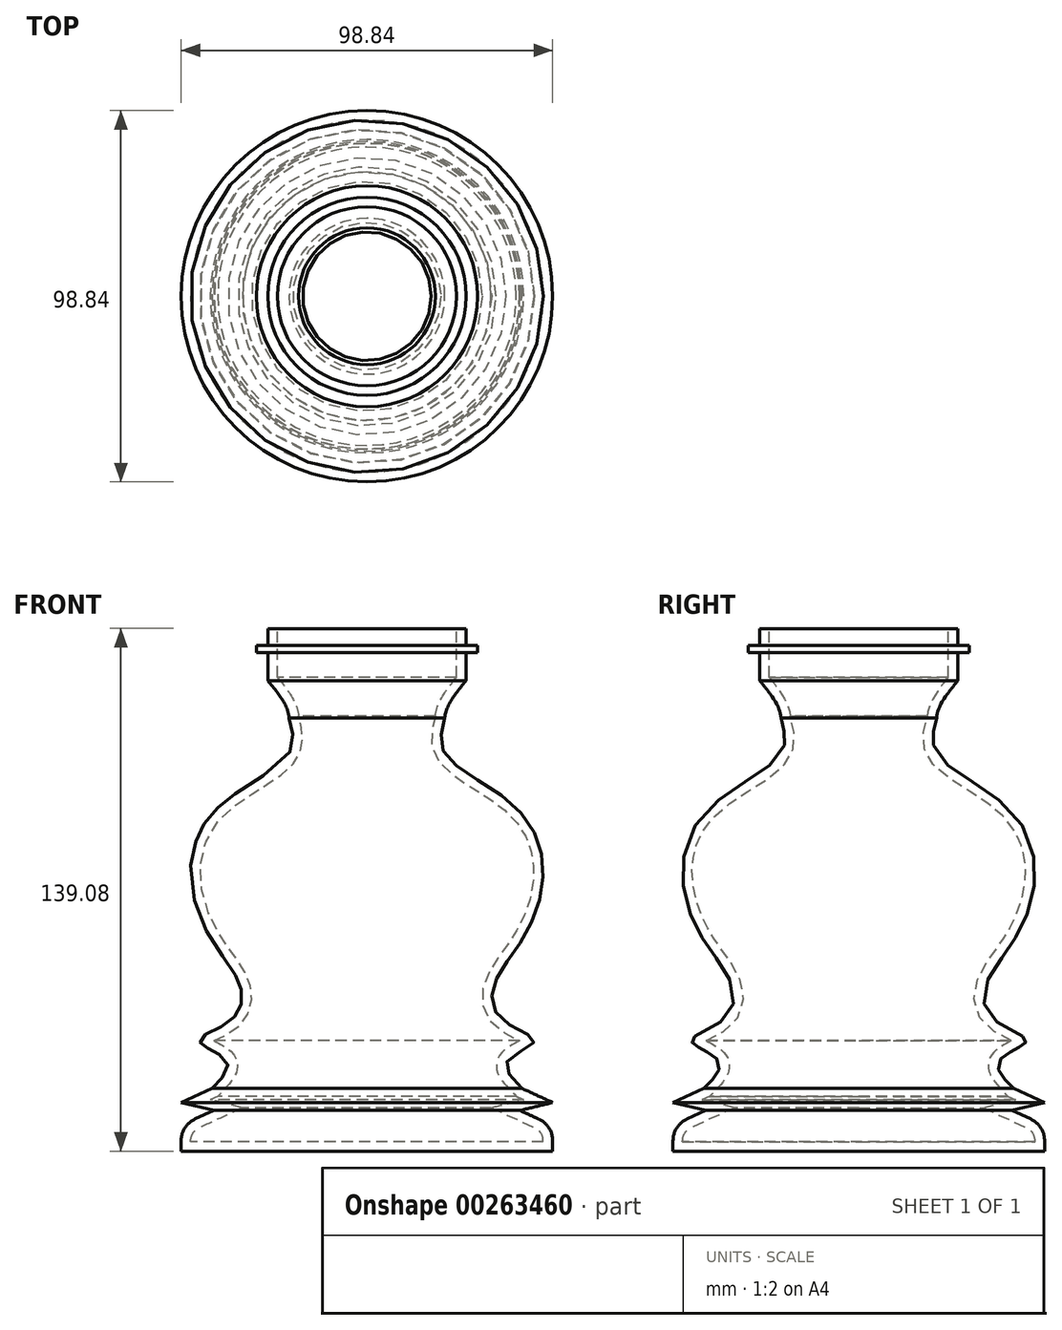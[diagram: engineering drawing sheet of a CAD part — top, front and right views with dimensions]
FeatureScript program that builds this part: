
annotation { "Feature Type Name" : "Feature", "Feature Type Description" : "" }
export const myFeature = defineFeature(function(context is Context, id is Id, definition is map)
    precondition{}
    {
        {
            var Q0;
            Q0=qCreatedBy(makeId("Front.planeOp"),FACE);
            var sketch = newSketch(context, id + "F0", { "sketchPlane" : qUnion([Q0])});
            skLineSegment(sketch, "E0", {"start": v(0, -75.54) * mm, "end": v(-49.42, -75.54) * mm});
            skLineSegment(sketch, "E1", {"start": v(-49.42, -75.54) * mm, "end": v(-49.42, -72.79) * mm});
            skLineSegment(sketch, "E2", {"start": v(-45.72, -67.01) * mm, "end": v(-40.71, -64.71) * mm});
            skLineSegment(sketch, "E3", {"start": v(-40.71, -64.71) * mm, "end": v(-49.42, -62.6) * mm});
            skLineSegment(sketch, "E4", {"start": v(-49.42, -62.6) * mm, "end": v(-41.18, -58.83) * mm});
            skFitSpline(sketch, "E5", {"points": [v(-49.42, -45.42) * mm, v(-39.06, -34.6) * mm, v(-49.42, -13.18) * mm, v(-42.36, 18.6) * mm, v(-25.65, 31.77) * mm, v(-20.7, 39.77) * mm, v(-26.36, 49.65) * mm], "startDerivative": vector(101.2, 64.64) * mm, "endDerivative": vector(-62.4, 76.27) * mm});
            skLineSegment(sketch, "E6", {"start": v(-26.36, 49.65) * mm, "end": v(-26.36, 57.18) * mm});
            skLineSegment(sketch, "E7", {"start": v(-26.36, 57.18) * mm, "end": v(-29.42, 57.18) * mm});
            skLineSegment(sketch, "E8", {"start": v(-29.42, 57.18) * mm, "end": v(-29.42, 59.07) * mm});
            skLineSegment(sketch, "E9", {"start": v(-29.42, 59.07) * mm, "end": v(-26.36, 59.07) * mm});
            skLineSegment(sketch, "E10", {"start": v(-26.36, 59.07) * mm, "end": v(-26.36, 63.54) * mm});
            skLineSegment(sketch, "E11", {"start": v(-26.36, 63.54) * mm, "end": v(0, 63.54) * mm});
            skLineSegment(sketch, "E12", {"start": v(0, 63.54) * mm, "end": v(0, -75.54) * mm});
            skPoint(sketch, "E13.visualSharp", {"position": v(-49.42, -56.24) * mm});
            skPoint(sketch, "E14.visualSharp", {"position": v(-49.42, -68.71) * mm});
            skArc(sketch, "E14.filletArc", {"start": v(-45.72, -67.01) * mm, "mid": v(-48.41, -69.36) * mm, "end": v(-49.42, -72.79) * mm});
            skFitSpline(sketch, "E15", {"points": [v(-20.7, 39.77) * mm, v(-20.7, 30.3) * mm, v(-38.75, 16.74) * mm, v(-46.88, 0) * mm, v(-41.88, -18.4) * mm, v(-33.61, -31.79) * mm, v(-36.23, -40.76) * mm, v(-44.53, -46.27) * mm, v(-37.32, -51.58) * mm, v(-41.18, -58.83) * mm], "startDerivative": vector(28.95, -103.5) * mm, "endDerivative": vector(-87.82, -88) * mm});
            skPoint(sketch, "E13.filletArc.center.orphan", {"position": v(-43.07, -51.58) * mm});
            skSolve(sketch);
        }
        {
            var Q0;
            Q0=makeQuery(id+"F0.imprint","IMPRINT",FACE,{"disambiguationData":[TD([[makeQuery(id+"F0.imprint","IMPRINT",EDGE,{"derivedFrom":sQuery(id+"F0.wireOp",EDGE,"E0")}),-1.0]])]});
            var Q1;
            Q1=sQuery(id+"F0.wireOp",EDGE,"E12");
            revolve(context, id + "F1", {"entities" : qUnion([Q0]), "axis" : qUnion([Q1]), "revolveType" : RevolveType.FULL});
        }
        {
            var Q0;
            Q0=makeQuery(id+"F1.opRevolve","SWEPT_FACE",FACE,{"disambiguationData":[OSD([sQuery(id+"F0.wireOp",EDGE,"E11")])]});
            shell(context, id + "F2", {"entities" : qUnion([Q0]), "thickness" : 2.54 * mm});
        }
    });
